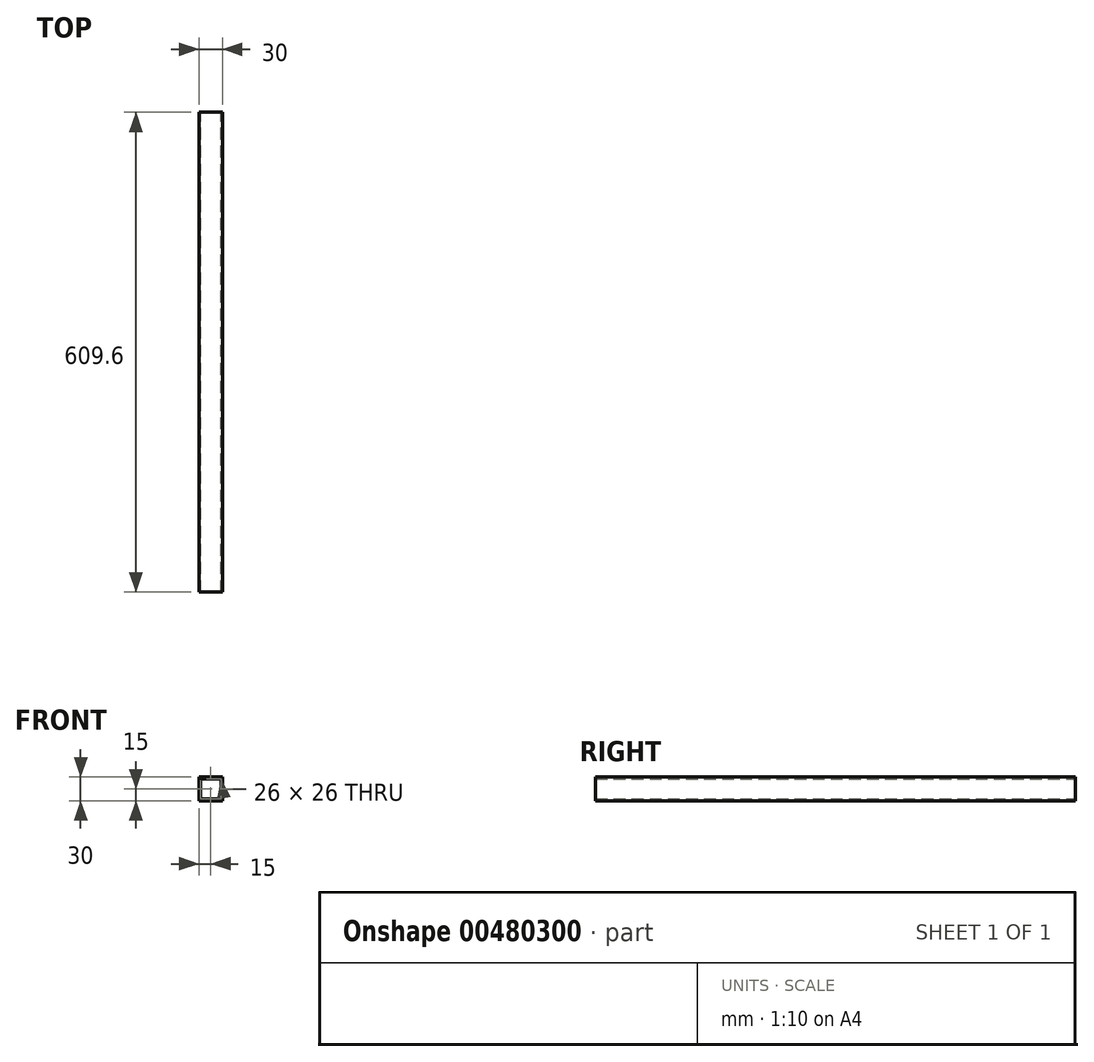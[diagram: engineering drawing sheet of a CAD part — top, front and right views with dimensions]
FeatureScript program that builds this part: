
annotation { "Feature Type Name" : "Feature", "Feature Type Description" : "" }
export const myFeature = defineFeature(function(context is Context, id is Id, definition is map)
    precondition{}
    {
        {
            var Q0;
            Q0=qCreatedBy(makeId("Front.planeOp"),FACE);
            var sketch = newSketch(context, id + "F0", { "sketchPlane" : qUnion([Q0])});
            skLineSegment(sketch, "E0.bottom", {"start": v(15, 15) * mm, "end": v(-15, 15) * mm});
            skLineSegment(sketch, "E0.top", {"start": v(15, -15) * mm, "end": v(-15, -15) * mm});
            skLineSegment(sketch, "E0.left", {"start": v(15, 15) * mm, "end": v(15, -15) * mm});
            skLineSegment(sketch, "E0.right", {"start": v(-15, 15) * mm, "end": v(-15, -15) * mm});
            skPoint(sketch, "E0.middle", {"position": v(0, 0) * mm});
            skLineSegment(sketch, "E1.0", {"start": v(-13, 13) * mm, "end": v(-13, -13) * mm});
            skLineSegment(sketch, "E1.1", {"start": v(13, 13) * mm, "end": v(-13, 13) * mm});
            skLineSegment(sketch, "E1.2", {"start": v(13, 13) * mm, "end": v(13, -13) * mm});
            skLineSegment(sketch, "E1.3", {"start": v(13, -13) * mm, "end": v(-13, -13) * mm});
            skSolve(sketch);
        }
        {
            var Q0;
            Q0=makeQuery(id+"F0.imprint","IMPRINT",FACE,{"disambiguationData":[TD([[makeQuery(id+"F0.imprint","IMPRINT",EDGE,{"derivedFrom":sQuery(id+"F0.wireOp",EDGE,"E0.bottom")}),1.0]])]});
            extrude(context, id + "F1", {"entities" : qUnion([Q0]), "endBound" : BoundingType.SYMMETRIC, "depth" : 609.6 * mm});
        }
    });
